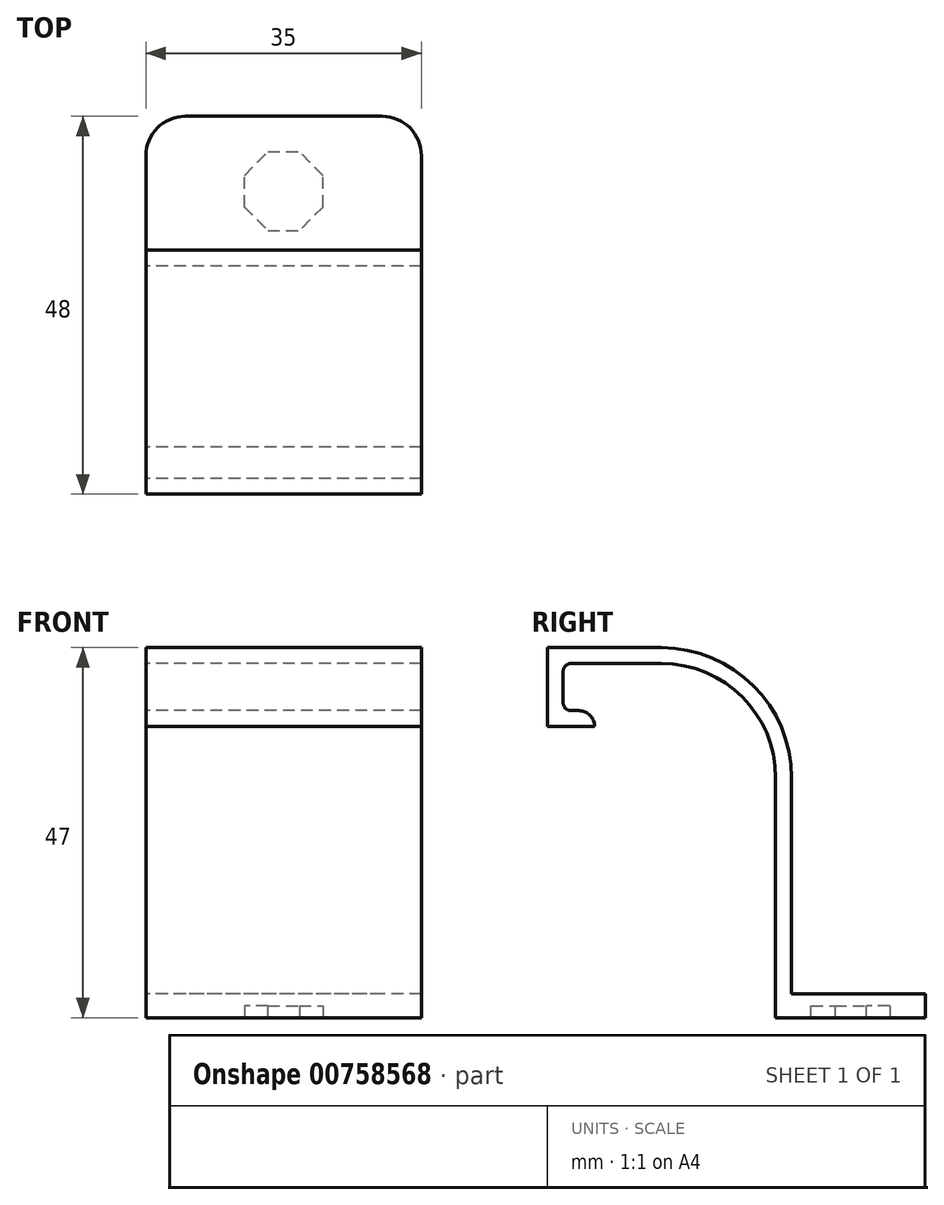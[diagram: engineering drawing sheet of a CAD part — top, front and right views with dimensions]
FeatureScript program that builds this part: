
annotation { "Feature Type Name" : "Feature", "Feature Type Description" : "" }
export const myFeature = defineFeature(function(context is Context, id is Id, definition is map)
    precondition{}
    {
        {
            var Q0;
            Q0=qCreatedBy(makeId("Right.planeOp"),FACE);
            var sketch = newSketch(context, id + "F0", { "sketchPlane" : qUnion([Q0])});
            skLineSegment(sketch, "E0", {"start": v(-28, 45) * mm, "end": v(-16.5, 45) * mm});
            skLineSegment(sketch, "E1", {"start": v(-2, 30.5) * mm, "end": v(-2, 0) * mm});
            skPoint(sketch, "E2.visualSharp", {"position": v(-2, 45) * mm});
            skArc(sketch, "E2.filletArc", {"start": v(-2, 30.5) * mm, "mid": v(-6.25, 40.75) * mm, "end": v(-16.5, 45) * mm});
            skLineSegment(sketch, "E3", {"start": v(-29, 44) * mm, "end": v(-29, 40) * mm});
            skLineSegment(sketch, "E4.0", {"start": v(-31, 47) * mm, "end": v(-31, 37) * mm});
            skLineSegment(sketch, "E4.1", {"start": v(-31, 47) * mm, "end": v(-16.5, 47) * mm});
            skArc(sketch, "E4.2", {"start": v(0, 30.5) * mm, "mid": v(-4.83, 42.17) * mm, "end": v(-16.5, 47) * mm});
            skLineSegment(sketch, "E4.3", {"start": v(0, 30.5) * mm, "end": v(0, 0) * mm});
            skLineSegment(sketch, "E5", {"start": v(-2, 0) * mm, "end": v(0, 0) * mm});
            skLineSegment(sketch, "E6", {"start": v(-31, 37) * mm, "end": v(-25, 37) * mm});
            skLineSegment(sketch, "E7", {"start": v(-25, 37) * mm, "end": v(-25, 37) * mm});
            skLineSegment(sketch, "E8", {"start": v(-27, 39) * mm, "end": v(-28, 39) * mm});
            skPoint(sketch, "E9.visualSharp", {"position": v(-29, 45) * mm});
            skArc(sketch, "E9.filletArc", {"start": v(-28, 45) * mm, "mid": v(-28.7, 44.7) * mm, "end": v(-29, 44) * mm});
            skPoint(sketch, "E10.visualSharp", {"position": v(-29, 39) * mm});
            skArc(sketch, "E10.filletArc", {"start": v(-29, 40) * mm, "mid": v(-28.7, 39.3) * mm, "end": v(-28, 39) * mm});
            skPoint(sketch, "E11.visualSharp", {"position": v(-25, 39) * mm});
            skArc(sketch, "E11.filletArc", {"start": v(-25, 37) * mm, "mid": v(-25.59, 38.41) * mm, "end": v(-27, 39) * mm});
            skSolve(sketch);
        }
        {
            var Q0;
            Q0=makeQuery(id+"F0.imprint","IMPRINT",FACE,{"disambiguationData":[TD([[makeQuery(id+"F0.imprint","IMPRINT",EDGE,{"derivedFrom":sQuery(id+"F0.wireOp",EDGE,"E0")}),1.0]])]});
            extrude(context, id + "F1", {"entities" : qUnion([Q0]), "depth" : 35 * mm, "offsetDistance" : 25 * mm});
        }
        {
            var Q0;
            Q0=makeQuery(id+"F1.opExtrude","SWEPT_FACE",FACE,{"disambiguationData":[OSD([sQuery(id+"F0.wireOp",EDGE,"E4.3")])]});
            var sketch = newSketch(context, id + "F2", { "sketchPlane" : qUnion([Q0])});
            skLineSegment(sketch, "E12", {"start": v(-35, 3) * mm, "end": v(0, 3) * mm});
            skSolve(sketch);
        }
        {
            var Q0;
            {var subQ0=sQuery(id+"F2.wireOp",EDGE,"E12");Q0=makeQuery(id+"F2.imprint","IMPRINT",FACE,{"disambiguationData":[TD([[makeQuery(id+"F2.imprint","IMPRINT",EDGE,{"derivedFrom":subQ0}),-1.0]])]});}
            extrude(context, id + "F3", {"entities" : qUnion([Q0]), "operationType" : NewBodyOperationType.ADD, "depth" : 17 * mm, "offsetDistance" : 25 * mm});
        }
        {
            var Q0;
            {var subQ0=sQuery(id+"F0.wireOp",EDGE,"E5");Q0=makeQuery(id+"F3.boolean.opBoolean","MERGE",FACE,{"derivedFrom":[makeQuery(id+"F1.opExtrude","SWEPT_FACE",FACE,{"disambiguationData":[OSD([subQ0])]}),makeQuery(id+"F3.opExtrude","SWEPT_FACE",FACE,{"disambiguationData":[OSD([sQuery(id+"F0.wireOp",EDGE,"E4.3"),subQ0])]})]});}
            var sketch = newSketch(context, id + "F4", { "sketchPlane" : qUnion([Q0])});
            skLineSegment(sketch, "E13.bottom", {"start": v(12.5, -2.5) * mm, "end": v(22.5, -2.5) * mm});
            skLineSegment(sketch, "E13.top", {"start": v(12.5, -12.5) * mm, "end": v(22.5, -12.5) * mm});
            skLineSegment(sketch, "E13.left", {"start": v(12.5, -2.5) * mm, "end": v(12.5, -12.5) * mm});
            skLineSegment(sketch, "E13.right", {"start": v(22.5, -2.5) * mm, "end": v(22.5, -12.5) * mm});
            skPoint(sketch, "E13.middle", {"position": v(17.5, -7.5) * mm});
            skLineSegment(sketch, "E14", {"start": v(35, -7.5) * mm, "end": v(0, -7.5) * mm, "construction": true});
            skLineSegment(sketch, "E15", {"start": v(17.5, 2) * mm, "end": v(17.5, -17) * mm, "construction": true});
            skSolve(sketch);
        }
        {
            var Q0;
            Q0=makeQuery(id+"F4.imprint","IMPRINT",FACE,{"disambiguationData":[TD([[makeQuery(id+"F4.imprint","IMPRINT",EDGE,{"derivedFrom":sQuery(id+"F4.wireOp",EDGE,"E13.bottom")}),-1.0]])]});
            extrude(context, id + "F5", {"entities" : qUnion([Q0]), "operationType" : NewBodyOperationType.REMOVE, "oppositeDirection" : true, "depth" : 1.5 * mm, "offsetDistance" : 25 * mm});
        }
        {
            var Q0;
            Q0=makeQuery(id+"F5.boolean.opBoolean","COPY",EDGE,{"derivedFrom":makeQuery(id+"F5.opExtrude","SWEPT_EDGE",EDGE,{"disambiguationData":[OSD([sQuery(id+"F4.wireOp",EDGE,"E13.bottom"),sQuery(id+"F4.wireOp",EDGE,"E13.right")])]})});
            var Q1;
            Q1=makeQuery(id+"F5.boolean.opBoolean","COPY",EDGE,{"derivedFrom":makeQuery(id+"F5.opExtrude","SWEPT_EDGE",EDGE,{"disambiguationData":[OSD([sQuery(id+"F4.wireOp",EDGE,"E13.top"),sQuery(id+"F4.wireOp",EDGE,"E13.right")])]})});
            var Q2;
            Q2=makeQuery(id+"F5.boolean.opBoolean","COPY",EDGE,{"derivedFrom":makeQuery(id+"F5.opExtrude","SWEPT_EDGE",EDGE,{"disambiguationData":[OSD([sQuery(id+"F4.wireOp",EDGE,"E13.top"),sQuery(id+"F4.wireOp",EDGE,"E13.left")])]})});
            var Q3;
            Q3=makeQuery(id+"F5.boolean.opBoolean","COPY",EDGE,{"derivedFrom":makeQuery(id+"F5.opExtrude","SWEPT_EDGE",EDGE,{"disambiguationData":[OSD([sQuery(id+"F4.wireOp",EDGE,"E13.bottom"),sQuery(id+"F4.wireOp",EDGE,"E13.left")])]})});
            chamfer(context, id + "F6", {"entities" : qUnion([Q0, Q1, Q2, Q3]), "width" : 3 * mm, "tangentPropagation" : true});
        }
        {
            var Q0;
            {var subQ0=sQuery(id+"F0.wireOp",EDGE,"E4.3");var subQ1=makeQuery(id+"F1.opExtrude","CAP_EDGE",EDGE,{"disambiguationData":[OSD([subQ0])],"isStart":true});Q0=makeQuery(id+"F3.opExtrude","CAP_EDGE",EDGE,{"disambiguationData":[OSD([subQ0]),TDD([makeQuery(id+"F2.imprint","IMPRINT",EDGE,{"disambiguationData":[TD([[makeQuery(id+"F2.imprint","INTERSECT",VERTEX,{"derivedFrom":[subQ1,sQuery(id+"F2.wireOp",EDGE,"E12")]}),-1.0]])],"derivedFrom":subQ1})])],"isStart":false});}
            var Q1;
            {var subQ0=sQuery(id+"F0.wireOp",EDGE,"E4.3");var subQ1=makeQuery(id+"F1.opExtrude","CAP_EDGE",EDGE,{"disambiguationData":[OSD([subQ0])],"isStart":false});Q1=makeQuery(id+"F3.opExtrude","CAP_EDGE",EDGE,{"disambiguationData":[OSD([subQ0]),TDD([makeQuery(id+"F2.imprint","IMPRINT",EDGE,{"disambiguationData":[TD([[makeQuery(id+"F2.imprint","INTERSECT",VERTEX,{"derivedFrom":[subQ1,sQuery(id+"F2.wireOp",EDGE,"E12")]}),-1.0]])],"derivedFrom":subQ1})])],"isStart":false});}
            var Q2;
            Q2=makeQuery(id+"F3.opExtrude","CAP_EDGE",EDGE,{"disambiguationData":[OSD([sQuery(id+"F2.wireOp",EDGE,"E12")])],"isStart":true});
            fillet(context, id + "F7", {"entities" : qUnion([Q0, Q1, Q2]), "radius" : 5 * mm, "tangentPropagation" : true, "allowEdgeOverflow" : false});
        }
    });
